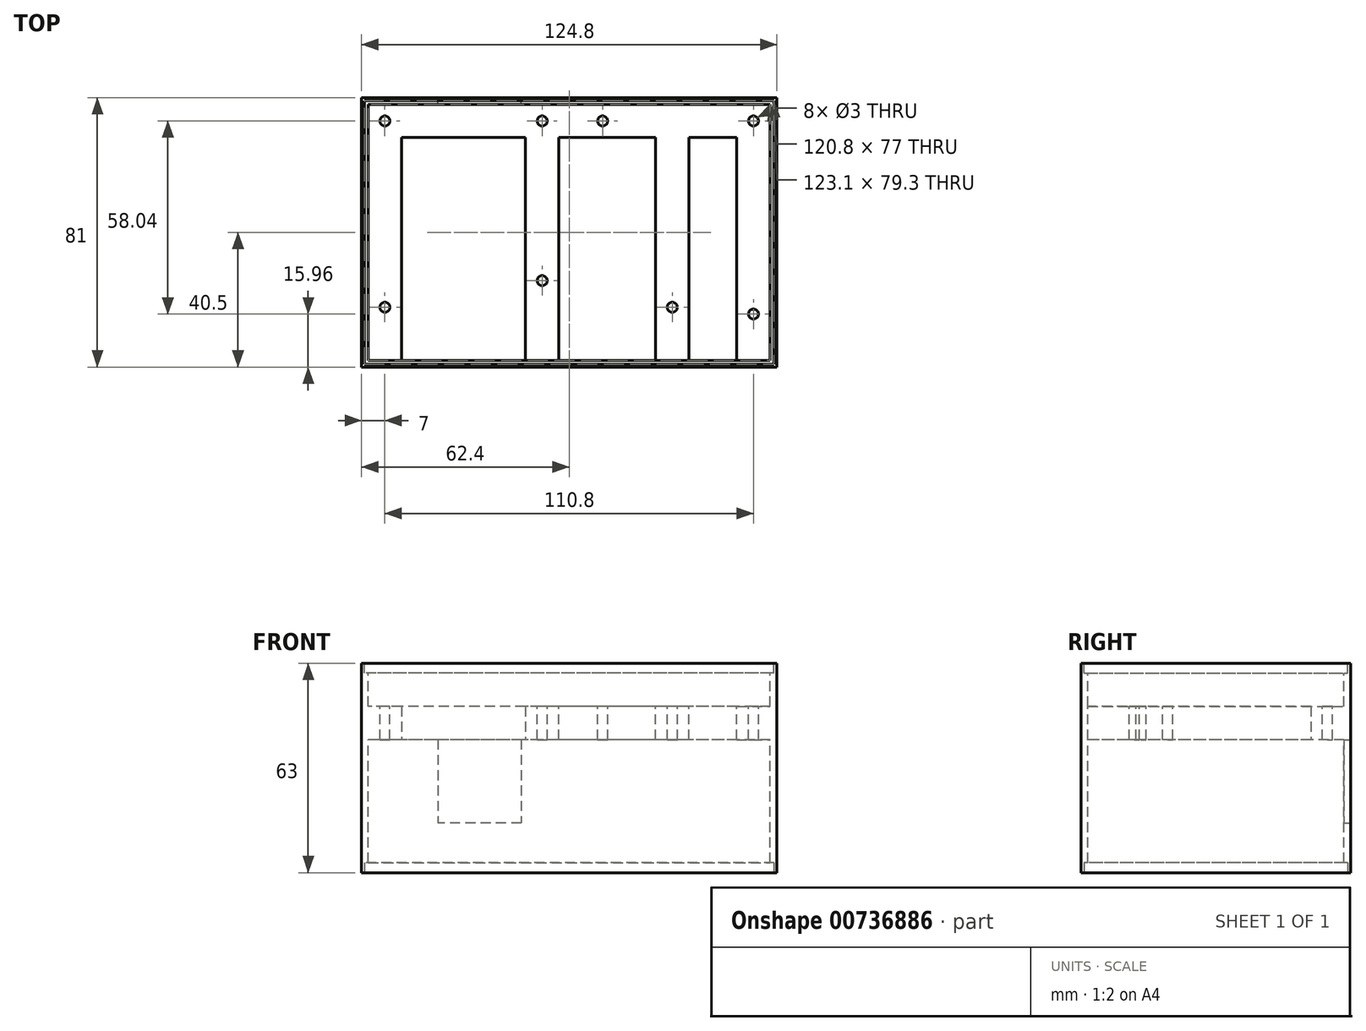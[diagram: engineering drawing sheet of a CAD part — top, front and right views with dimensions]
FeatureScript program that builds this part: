
annotation { "Feature Type Name" : "Feature", "Feature Type Description" : "" }
export const myFeature = defineFeature(function(context is Context, id is Id, definition is map)
    precondition{}
    {
        {
            var Q0;
            Q0=qCreatedBy(makeId("Top.planeOp"),FACE);
            var sketch = newSketch(context, id + "F0", { "sketchPlane" : qUnion([Q0])});
            skLineSegment(sketch, "E0.bottom", {"start": v(62.4, -40.5) * mm, "end": v(-62.4, -40.5) * mm});
            skLineSegment(sketch, "E0.top", {"start": v(62.4, 40.5) * mm, "end": v(-62.4, 40.5) * mm});
            skLineSegment(sketch, "E0.left", {"start": v(62.4, -40.5) * mm, "end": v(62.4, 40.5) * mm});
            skLineSegment(sketch, "E0.right", {"start": v(-62.4, -40.5) * mm, "end": v(-62.4, 40.5) * mm});
            skPoint(sketch, "E0.middle", {"position": v(0, 0) * mm});
            skSolve(sketch);
        }
        {
            var Q0;
            Q0=makeQuery(id+"F0.imprint","IMPRINT",FACE,{"disambiguationData":[TD([[makeQuery(id+"F0.imprint","IMPRINT",EDGE,{"derivedFrom":sQuery(id+"F0.wireOp",EDGE,"E0.bottom")}),-1.0]])]});
            extrude(context, id + "F1", {"entities" : qUnion([Q0]), "depth" : 63 * mm, "offsetDistance" : 25 * mm});
        }
        {
            var Q0;
            Q0=makeQuery(id+"F1.opExtrude","CAP_FACE",FACE,{"disambiguationData":[OSD([sQuery(id+"F0.wireOp",EDGE,"E0.bottom"),sQuery(id+"F0.wireOp",EDGE,"E0.top"),sQuery(id+"F0.wireOp",EDGE,"E0.left"),sQuery(id+"F0.wireOp",EDGE,"E0.right")])],"isStart":false});
            var sketch = newSketch(context, id + "F2", { "sketchPlane" : qUnion([Q0])});
            skLineSegment(sketch, "E1.bottom", {"start": v(61.55, -39.65) * mm, "end": v(-61.55, -39.65) * mm});
            skLineSegment(sketch, "E1.top", {"start": v(61.55, 39.65) * mm, "end": v(-61.55, 39.65) * mm});
            skLineSegment(sketch, "E1.left", {"start": v(61.55, -39.65) * mm, "end": v(61.55, 39.65) * mm});
            skLineSegment(sketch, "E1.right", {"start": v(-61.55, -39.65) * mm, "end": v(-61.55, 39.65) * mm});
            skPoint(sketch, "E1.middle", {"position": v(0, 0) * mm});
            skSolve(sketch);
        }
        {
            var Q0;
            Q0 = qSketchRegion(id + "F2", true);
            extrude(context, id + "F3", {"entities" : qUnion([Q0]), "operationType" : NewBodyOperationType.REMOVE, "oppositeDirection" : true, "depth" : 3 * mm, "offsetDistance" : 25 * mm});
        }
        {
            var Q0;
            Q0=makeQuery(id+"F1.opExtrude","CAP_FACE",FACE,{"disambiguationData":[OSD([sQuery(id+"F0.wireOp",EDGE,"E0.bottom"),sQuery(id+"F0.wireOp",EDGE,"E0.top"),sQuery(id+"F0.wireOp",EDGE,"E0.left"),sQuery(id+"F0.wireOp",EDGE,"E0.right")])],"isStart":true});
            var sketch = newSketch(context, id + "F4", { "sketchPlane" : qUnion([Q0])});
            skLineSegment(sketch, "E2.bottom", {"start": v(61.55, -39.65) * mm, "end": v(-61.55, -39.65) * mm});
            skLineSegment(sketch, "E2.top", {"start": v(61.55, 39.65) * mm, "end": v(-61.55, 39.65) * mm});
            skLineSegment(sketch, "E2.left", {"start": v(61.55, -39.65) * mm, "end": v(61.55, 39.65) * mm});
            skLineSegment(sketch, "E2.right", {"start": v(-61.55, -39.65) * mm, "end": v(-61.55, 39.65) * mm});
            skPoint(sketch, "E2.middle", {"position": v(0, 0) * mm});
            skSolve(sketch);
        }
        {
            var Q0;
            Q0 = qSketchRegion(id + "F4", true);
            extrude(context, id + "F5", {"entities" : qUnion([Q0]), "operationType" : NewBodyOperationType.REMOVE, "oppositeDirection" : true, "depth" : 3 * mm, "offsetDistance" : 25 * mm});
        }
        {
            var Q0;
            Q0=makeQuery(id+"F3.boolean.opBoolean","COPY",FACE,{"derivedFrom":makeQuery(id+"F3.opExtrude","CAP_FACE",FACE,{"disambiguationData":[OSD([sQuery(id+"F2.wireOp",EDGE,"E1.bottom"),sQuery(id+"F2.wireOp",EDGE,"E1.top"),sQuery(id+"F2.wireOp",EDGE,"E1.left"),sQuery(id+"F2.wireOp",EDGE,"E1.right")])],"isStart":false})});
            var sketch = newSketch(context, id + "F6", { "sketchPlane" : qUnion([Q0])});
            skLineSegment(sketch, "E3.bottom", {"start": v(60.4, -38.5) * mm, "end": v(-60.4, -38.5) * mm});
            skLineSegment(sketch, "E3.top", {"start": v(60.4, 38.5) * mm, "end": v(-60.4, 38.5) * mm});
            skLineSegment(sketch, "E3.left", {"start": v(60.4, -38.5) * mm, "end": v(60.4, 38.5) * mm});
            skLineSegment(sketch, "E3.right", {"start": v(-60.4, -38.5) * mm, "end": v(-60.4, 38.5) * mm});
            skPoint(sketch, "E3.middle", {"position": v(0, 0) * mm});
            skSolve(sketch);
        }
        {
            var Q0;
            Q0 = qSketchRegion(id + "F6", true);
            extrude(context, id + "F7", {"entities" : qUnion([Q0]), "operationType" : NewBodyOperationType.REMOVE, "endBound" : BoundingType.THROUGH_ALL, "oppositeDirection" : true, "depth" : 25 * mm, "offsetDistance" : 25 * mm});
        }
        {
            var Q0;
            Q0=makeQuery(id+"F1.opExtrude","SWEPT_FACE",FACE,{"disambiguationData":[OSD([sQuery(id+"F0.wireOp",EDGE,"E0.bottom")])]});
            var sketch = newSketch(context, id + "F8", { "sketchPlane" : qUnion([Q0])});
            skLineSegment(sketch, "E4.bottom", {"start": v(-62.4, 50) * mm, "end": v(-50.4, 50) * mm});
            skLineSegment(sketch, "E4.top", {"start": v(-62.4, 40) * mm, "end": v(-50.4, 40) * mm});
            skLineSegment(sketch, "E4.left", {"start": v(-62.4, 50) * mm, "end": v(-62.4, 40) * mm});
            skLineSegment(sketch, "E4.right", {"start": v(-50.4, 50) * mm, "end": v(-50.4, 40) * mm});
            skSolve(sketch);
        }
        {
            var Q0;
            Q0 = qSketchRegion(id + "F8", true);
            extrude(context, id + "F9", {"entities" : qUnion([Q0]), "operationType" : NewBodyOperationType.ADD, "oppositeDirection" : true, "depth" : 81 * mm, "offsetDistance" : 25 * mm});
        }
        {
            var Q0;
            Q0=makeQuery(id+"F1.opExtrude","SWEPT_FACE",FACE,{"disambiguationData":[OSD([sQuery(id+"F0.wireOp",EDGE,"E0.bottom")])]});
            var sketch = newSketch(context, id + "F10", { "sketchPlane" : qUnion([Q0])});
            skLineSegment(sketch, "E5.bottom", {"start": v(62.4, 50) * mm, "end": v(50.4, 50) * mm});
            skLineSegment(sketch, "E5.top", {"start": v(62.4, 40) * mm, "end": v(50.4, 40) * mm});
            skLineSegment(sketch, "E5.left", {"start": v(62.4, 50) * mm, "end": v(62.4, 40) * mm});
            skLineSegment(sketch, "E5.right", {"start": v(50.4, 50) * mm, "end": v(50.4, 40) * mm});
            skSolve(sketch);
        }
        {
            var Q0;
            Q0 = qSketchRegion(id + "F10", true);
            extrude(context, id + "F11", {"entities" : qUnion([Q0]), "operationType" : NewBodyOperationType.ADD, "oppositeDirection" : true, "depth" : 81 * mm, "offsetDistance" : 25 * mm});
        }
        {
            var Q0;
            Q0=makeQuery(id+"F1.opExtrude","SWEPT_FACE",FACE,{"disambiguationData":[OSD([sQuery(id+"F0.wireOp",EDGE,"E0.right")])]});
            var sketch = newSketch(context, id + "F12", { "sketchPlane" : qUnion([Q0])});
            skLineSegment(sketch, "E6.bottom", {"start": v(-40.5, 50) * mm, "end": v(-28.5, 50) * mm});
            skLineSegment(sketch, "E6.top", {"start": v(-40.5, 40) * mm, "end": v(-28.5, 40) * mm});
            skLineSegment(sketch, "E6.left", {"start": v(-40.5, 50) * mm, "end": v(-40.5, 40) * mm});
            skLineSegment(sketch, "E6.right", {"start": v(-28.5, 50) * mm, "end": v(-28.5, 40) * mm});
            skSolve(sketch);
        }
        {
            var Q0;
            Q0 = qSketchRegion(id + "F12", true);
            extrude(context, id + "F13", {"entities" : qUnion([Q0]), "operationType" : NewBodyOperationType.ADD, "oppositeDirection" : true, "depth" : 124.8 * mm, "offsetDistance" : 25 * mm});
        }
        {
            var Q0;
            Q0=makeQuery(id+"F13.boolean.opBoolean","MERGE",FACE,{"derivedFrom":[makeQuery(id+"F9.opExtrude","SWEPT_FACE",FACE,{"disambiguationData":[OSD([sQuery(id+"F8.wireOp",EDGE,"E4.bottom")])]}),makeQuery(id+"F11.opExtrude","SWEPT_FACE",FACE,{"disambiguationData":[OSD([sQuery(id+"F10.wireOp",EDGE,"E5.bottom")])]}),makeQuery(id+"F13.opExtrude","SWEPT_FACE",FACE,{"disambiguationData":[OSD([sQuery(id+"F12.wireOp",EDGE,"E6.bottom")])]})]});
            var sketch = newSketch(context, id + "F14", { "sketchPlane" : qUnion([Q0])});
            skCircle(sketch, "E7", {"center": v(-55.4, 33.5) * mm, "radius": 1.5 * mm});
            skSolve(sketch);
        }
        {
            var Q0;
            Q0 = qSketchRegion(id + "F14", true);
            extrude(context, id + "F15", {"entities" : qUnion([Q0]), "operationType" : NewBodyOperationType.REMOVE, "endBound" : BoundingType.THROUGH_ALL, "oppositeDirection" : true, "depth" : 25 * mm, "offsetDistance" : 25 * mm});
        }
        {
            var Q0;
            Q0=makeQuery(id+"F13.boolean.opBoolean","MERGE",FACE,{"derivedFrom":[makeQuery(id+"F9.opExtrude","SWEPT_FACE",FACE,{"disambiguationData":[OSD([sQuery(id+"F8.wireOp",EDGE,"E4.bottom")])]}),makeQuery(id+"F11.opExtrude","SWEPT_FACE",FACE,{"disambiguationData":[OSD([sQuery(id+"F10.wireOp",EDGE,"E5.bottom")])]}),makeQuery(id+"F13.opExtrude","SWEPT_FACE",FACE,{"disambiguationData":[OSD([sQuery(id+"F12.wireOp",EDGE,"E6.bottom")])]})]});
            var sketch = newSketch(context, id + "F16", { "sketchPlane" : qUnion([Q0])});
            skCircle(sketch, "E8", {"center": v(55.4, 33.5) * mm, "radius": 1.5 * mm});
            skSolve(sketch);
        }
        {
            var Q0;
            Q0 = qSketchRegion(id + "F16", true);
            extrude(context, id + "F17", {"entities" : qUnion([Q0]), "operationType" : NewBodyOperationType.REMOVE, "endBound" : BoundingType.THROUGH_ALL, "oppositeDirection" : true, "depth" : 25 * mm, "offsetDistance" : 25 * mm});
        }
        {
            var Q0;
            Q0=makeQuery(id+"F13.boolean.opBoolean","MERGE",FACE,{"derivedFrom":[makeQuery(id+"F9.opExtrude","SWEPT_FACE",FACE,{"disambiguationData":[OSD([sQuery(id+"F8.wireOp",EDGE,"E4.bottom")])]}),makeQuery(id+"F11.opExtrude","SWEPT_FACE",FACE,{"disambiguationData":[OSD([sQuery(id+"F10.wireOp",EDGE,"E5.bottom")])]}),makeQuery(id+"F13.opExtrude","SWEPT_FACE",FACE,{"disambiguationData":[OSD([sQuery(id+"F12.wireOp",EDGE,"E6.bottom")])]})]});
            var sketch = newSketch(context, id + "F18", { "sketchPlane" : qUnion([Q0])});
            skCircle(sketch, "E9", {"center": v(-55.4, -22.5) * mm, "radius": 1.5 * mm});
            skSolve(sketch);
        }
        {
            var Q0;
            Q0 = qSketchRegion(id + "F18", true);
            extrude(context, id + "F19", {"entities" : qUnion([Q0]), "operationType" : NewBodyOperationType.REMOVE, "endBound" : BoundingType.THROUGH_ALL, "oppositeDirection" : true, "depth" : 25 * mm, "offsetDistance" : 25 * mm});
        }
        {
            var Q0;
            Q0=makeQuery(id+"F13.boolean.opBoolean","MERGE",FACE,{"derivedFrom":[makeQuery(id+"F9.opExtrude","SWEPT_FACE",FACE,{"disambiguationData":[OSD([sQuery(id+"F8.wireOp",EDGE,"E4.bottom")])]}),makeQuery(id+"F11.opExtrude","SWEPT_FACE",FACE,{"disambiguationData":[OSD([sQuery(id+"F10.wireOp",EDGE,"E5.bottom")])]}),makeQuery(id+"F13.opExtrude","SWEPT_FACE",FACE,{"disambiguationData":[OSD([sQuery(id+"F12.wireOp",EDGE,"E6.bottom")])]})]});
            var sketch = newSketch(context, id + "F20", { "sketchPlane" : qUnion([Q0])});
            skCircle(sketch, "E10", {"center": v(-8.1, 33.5) * mm, "radius": 1.5 * mm});
            skSolve(sketch);
        }
        {
            var Q0;
            Q0 = qSketchRegion(id + "F20", true);
            extrude(context, id + "F21", {"entities" : qUnion([Q0]), "operationType" : NewBodyOperationType.REMOVE, "endBound" : BoundingType.THROUGH_ALL, "oppositeDirection" : true, "depth" : 25 * mm, "offsetDistance" : 25 * mm});
        }
        {
            var Q0;
            Q0=makeQuery(id+"F13.boolean.opBoolean","MERGE",FACE,{"derivedFrom":[makeQuery(id+"F9.opExtrude","SWEPT_FACE",FACE,{"disambiguationData":[OSD([sQuery(id+"F8.wireOp",EDGE,"E4.bottom")])]}),makeQuery(id+"F11.opExtrude","SWEPT_FACE",FACE,{"disambiguationData":[OSD([sQuery(id+"F10.wireOp",EDGE,"E5.bottom")])]}),makeQuery(id+"F13.opExtrude","SWEPT_FACE",FACE,{"disambiguationData":[OSD([sQuery(id+"F12.wireOp",EDGE,"E6.bottom")])]})]});
            var sketch = newSketch(context, id + "F22", { "sketchPlane" : qUnion([Q0])});
            skCircle(sketch, "E11", {"center": v(10.06, 33.5) * mm, "radius": 1.5 * mm});
            skSolve(sketch);
        }
        {
            var Q0;
            Q0 = qSketchRegion(id + "F22", true);
            extrude(context, id + "F23", {"entities" : qUnion([Q0]), "operationType" : NewBodyOperationType.REMOVE, "endBound" : BoundingType.THROUGH_ALL, "oppositeDirection" : true, "depth" : 25 * mm, "offsetDistance" : 25 * mm});
        }
        {
            var Q0;
            Q0=makeQuery(id+"F1.opExtrude","SWEPT_FACE",FACE,{"disambiguationData":[OSD([sQuery(id+"F0.wireOp",EDGE,"E0.bottom")])]});
            var sketch = newSketch(context, id + "F24", { "sketchPlane" : qUnion([Q0])});
            skLineSegment(sketch, "E12.bottom", {"start": v(26, 50) * mm, "end": v(36, 50) * mm});
            skLineSegment(sketch, "E12.top", {"start": v(26, 40) * mm, "end": v(36, 40) * mm});
            skLineSegment(sketch, "E12.left", {"start": v(26, 50) * mm, "end": v(26, 40) * mm});
            skLineSegment(sketch, "E12.right", {"start": v(36, 50) * mm, "end": v(36, 40) * mm});
            skSolve(sketch);
        }
        {
            var Q0;
            Q0 = qSketchRegion(id + "F24", true);
            extrude(context, id + "F25", {"entities" : qUnion([Q0]), "operationType" : NewBodyOperationType.ADD, "oppositeDirection" : true, "depth" : 81 * mm, "offsetDistance" : 25 * mm});
        }
        {
            var Q0;
            Q0=makeQuery(id+"F25.boolean.opBoolean","MERGE",FACE,{"derivedFrom":[makeQuery(id+"F13.boolean.opBoolean","MERGE",FACE,{"derivedFrom":[makeQuery(id+"F9.opExtrude","SWEPT_FACE",FACE,{"disambiguationData":[OSD([sQuery(id+"F8.wireOp",EDGE,"E4.bottom")])]}),makeQuery(id+"F11.opExtrude","SWEPT_FACE",FACE,{"disambiguationData":[OSD([sQuery(id+"F10.wireOp",EDGE,"E5.bottom")])]}),makeQuery(id+"F13.opExtrude","SWEPT_FACE",FACE,{"disambiguationData":[OSD([sQuery(id+"F12.wireOp",EDGE,"E6.bottom")])]})]}),makeQuery(id+"F25.opExtrude","SWEPT_FACE",FACE,{"disambiguationData":[OSD([sQuery(id+"F24.wireOp",EDGE,"E12.bottom")])]})]});
            var sketch = newSketch(context, id + "F26", { "sketchPlane" : qUnion([Q0])});
            skCircle(sketch, "E13", {"center": v(31, -22.5) * mm, "radius": 1.5 * mm});
            skSolve(sketch);
        }
        {
            var Q0;
            Q0 = qSketchRegion(id + "F26", true);
            extrude(context, id + "F27", {"entities" : qUnion([Q0]), "operationType" : NewBodyOperationType.REMOVE, "endBound" : BoundingType.THROUGH_ALL, "oppositeDirection" : true, "depth" : 25 * mm, "offsetDistance" : 25 * mm});
        }
        {
            var Q0;
            Q0=makeQuery(id+"F1.opExtrude","SWEPT_FACE",FACE,{"disambiguationData":[OSD([sQuery(id+"F0.wireOp",EDGE,"E0.bottom")])]});
            var sketch = newSketch(context, id + "F28", { "sketchPlane" : qUnion([Q0])});
            skLineSegment(sketch, "E14.bottom", {"start": v(-13.1, 50) * mm, "end": v(-3.1, 50) * mm});
            skLineSegment(sketch, "E14.top", {"start": v(-13.1, 40) * mm, "end": v(-3.1, 40) * mm});
            skLineSegment(sketch, "E14.left", {"start": v(-13.1, 50) * mm, "end": v(-13.1, 40) * mm});
            skLineSegment(sketch, "E14.right", {"start": v(-3.1, 50) * mm, "end": v(-3.1, 40) * mm});
            skSolve(sketch);
        }
        {
            var Q0;
            Q0 = qSketchRegion(id + "F28", true);
            extrude(context, id + "F29", {"entities" : qUnion([Q0]), "operationType" : NewBodyOperationType.ADD, "oppositeDirection" : true, "depth" : 69 * mm, "offsetDistance" : 25 * mm});
        }
        {
            var Q0;
            Q0=makeQuery(id+"F29.boolean.opBoolean","MERGE",FACE,{"derivedFrom":[makeQuery(id+"F25.boolean.opBoolean","MERGE",FACE,{"derivedFrom":[makeQuery(id+"F13.boolean.opBoolean","MERGE",FACE,{"derivedFrom":[makeQuery(id+"F9.opExtrude","SWEPT_FACE",FACE,{"disambiguationData":[OSD([sQuery(id+"F8.wireOp",EDGE,"E4.bottom")])]}),makeQuery(id+"F11.opExtrude","SWEPT_FACE",FACE,{"disambiguationData":[OSD([sQuery(id+"F10.wireOp",EDGE,"E5.bottom")])]}),makeQuery(id+"F13.opExtrude","SWEPT_FACE",FACE,{"disambiguationData":[OSD([sQuery(id+"F12.wireOp",EDGE,"E6.bottom")])]})]}),makeQuery(id+"F25.opExtrude","SWEPT_FACE",FACE,{"disambiguationData":[OSD([sQuery(id+"F24.wireOp",EDGE,"E12.bottom")])]})]}),makeQuery(id+"F29.opExtrude","SWEPT_FACE",FACE,{"disambiguationData":[OSD([sQuery(id+"F28.wireOp",EDGE,"E14.bottom")])]})]});
            var sketch = newSketch(context, id + "F30", { "sketchPlane" : qUnion([Q0])});
            skCircle(sketch, "E15", {"center": v(-8.1, -14.5) * mm, "radius": 1.5 * mm});
            skSolve(sketch);
        }
        {
            var Q0;
            Q0 = qSketchRegion(id + "F30", true);
            extrude(context, id + "F31", {"entities" : qUnion([Q0]), "operationType" : NewBodyOperationType.REMOVE, "endBound" : BoundingType.THROUGH_ALL, "oppositeDirection" : true, "depth" : 25 * mm, "offsetDistance" : 25 * mm});
        }
        {
            var Q0;
            Q0=makeQuery(id+"F1.opExtrude","SWEPT_FACE",FACE,{"disambiguationData":[OSD([sQuery(id+"F0.wireOp",EDGE,"E0.top")])]});
            var sketch = newSketch(context, id + "F32", { "sketchPlane" : qUnion([Q0])});
            skLineSegment(sketch, "E16.bottom", {"start": v(14.4, 40) * mm, "end": v(39.4, 40) * mm});
            skLineSegment(sketch, "E16.top", {"start": v(14.4, 15) * mm, "end": v(39.4, 15) * mm});
            skLineSegment(sketch, "E16.left", {"start": v(14.4, 40) * mm, "end": v(14.4, 15) * mm});
            skLineSegment(sketch, "E16.right", {"start": v(39.4, 40) * mm, "end": v(39.4, 15) * mm});
            skSolve(sketch);
        }
        {
            var Q0;
            Q0 = qSketchRegion(id + "F32", true);
            extrude(context, id + "F33", {"entities" : qUnion([Q0]), "operationType" : NewBodyOperationType.REMOVE, "oppositeDirection" : true, "depth" : 25 * mm, "offsetDistance" : 25 * mm});
        }
        {
            var Q0;
            Q0=makeQuery(id+"F29.boolean.opBoolean","MERGE",FACE,{"derivedFrom":[makeQuery(id+"F25.boolean.opBoolean","MERGE",FACE,{"derivedFrom":[makeQuery(id+"F13.boolean.opBoolean","MERGE",FACE,{"derivedFrom":[makeQuery(id+"F9.opExtrude","SWEPT_FACE",FACE,{"disambiguationData":[OSD([sQuery(id+"F8.wireOp",EDGE,"E4.bottom")])]}),makeQuery(id+"F11.opExtrude","SWEPT_FACE",FACE,{"disambiguationData":[OSD([sQuery(id+"F10.wireOp",EDGE,"E5.bottom")])]}),makeQuery(id+"F13.opExtrude","SWEPT_FACE",FACE,{"disambiguationData":[OSD([sQuery(id+"F12.wireOp",EDGE,"E6.bottom")])]})]}),makeQuery(id+"F25.opExtrude","SWEPT_FACE",FACE,{"disambiguationData":[OSD([sQuery(id+"F24.wireOp",EDGE,"E12.bottom")])]})]}),makeQuery(id+"F29.opExtrude","SWEPT_FACE",FACE,{"disambiguationData":[OSD([sQuery(id+"F28.wireOp",EDGE,"E14.bottom")])]})]});
            var sketch = newSketch(context, id + "F34", { "sketchPlane" : qUnion([Q0])});
            skCircle(sketch, "E17", {"center": v(55.4, -24.54) * mm, "radius": 1.5 * mm});
            skSolve(sketch);
        }
        {
            var Q0;
            Q0 = qSketchRegion(id + "F34", true);
            extrude(context, id + "F35", {"entities" : qUnion([Q0]), "operationType" : NewBodyOperationType.REMOVE, "endBound" : BoundingType.THROUGH_ALL, "oppositeDirection" : true, "depth" : 25 * mm, "offsetDistance" : 25 * mm});
        }
    });
